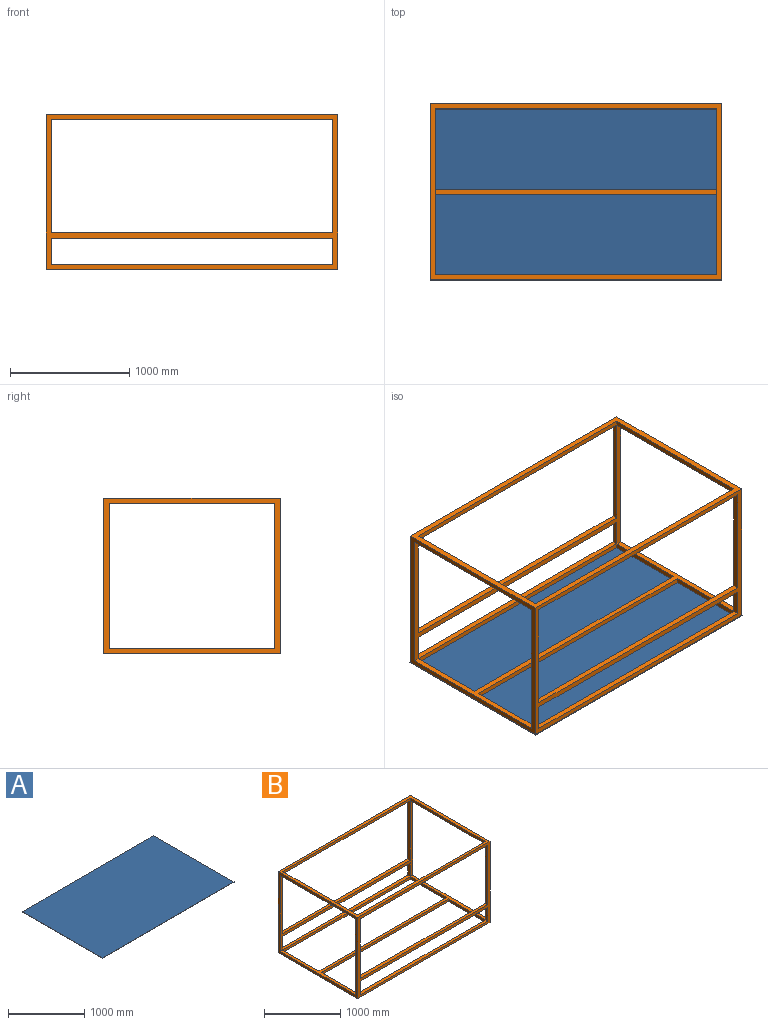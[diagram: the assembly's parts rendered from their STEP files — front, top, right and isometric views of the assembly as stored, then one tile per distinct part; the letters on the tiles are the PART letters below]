
ASSEMBLY  parts=2 mates=1
PART A: 6 faces, bbox 2450x1490x4 mm
  f0: plane 2450x4mm, normal (0,1,0), area 9800mm2, adj f1,f3,f4,f5
  f1: plane 1490x4mm, normal (-1,0,0), area 5960mm2, adj f0,f2,f4,f5
  f2: plane 2450x4mm, normal (0,-1,0), area 9800mm2, adj f1,f3,f4,f5
  f3: plane 1490x4mm, normal (1,0,0), area 5960mm2, adj f0,f2,f4,f5
  f4: plane 2450x1490mm, normal (0,0,1), area 3650500mm2, adj f0,f1,f2,f3
  f5: plane 2450x1490mm, normal (0,0,-1), area 3650500mm2, adj f0,f1,f2,f3
PART B: 39 faces, bbox 2450x1480x1300 mm
  f0: plane 955x45mm, normal (1,0,0), area 42975mm2, adj f14,f20,f26,f37
  f1: plane 955x45mm, normal (-1,0,0), area 42975mm2, adj f14,f20,f26,f37
  f2: plane 220x45mm, normal (1,0,0), area 9900mm2, adj f4,f17,f23,f36
  f3: plane 220x45mm, normal (-1,0,0), area 9900mm2, adj f4,f17,f23,f36
  f4: plane 2360x45mm, normal (0,0,1), area 106200mm2, adj f2,f3,f11,f17
  f5: plane 2450x1390mm, normal (0,0,1), area 231300mm2, adj f7,f9,f10,f12,f13,f15,f16,f18
  f6: plane 2360x45mm, normal (0,0,1), area 106200mm2, adj f8,f14,f21,f24
  f7: plane 670x40mm, normal (1,0,0), area 26800mm2, adj f5,f8,f18,f19
  f8: plane 2360x40mm, normal (0,-1,0), area 94400mm2, adj f6,f7,f9,f19
  f9: plane 670x40mm, normal (-1,0,0), area 26800mm2, adj f5,f8,f18,f19
  f10: plane 675x40mm, normal (-1,0,0), area 27000mm2, adj f5,f11,f16,f19
  f11: plane 2360x40mm, normal (0,1,0), area 94400mm2, adj f4,f10,f12,f19
  f12: plane 675x40mm, normal (1,0,0), area 27000mm2, adj f5,f11,f16,f19
  f13: plane 1480x1300mm, normal (1,0,0), area 228200mm2, adj f5,f14,f17,f19,f20,f23,f29,f34
  f14: plane 2450x1300mm, normal (0,1,0), area 412000mm2, adj f0,f1,f6,f13,f15,f19,f21,f24
  f15: plane 1480x1300mm, normal (-1,0,0), area 228200mm2, adj f5,f14,f17,f19,f20,f23,f28,f34
  f16: plane 2360x40mm, normal (0,-1,0), area 94400mm2, adj f5,f10,f12,f19
  f17: plane 2450x1300mm, normal (0,-1,0), area 412000mm2, adj f2,f3,f4,f13,f15,f19,f22,f25
  f18: plane 2360x40mm, normal (0,1,0), area 94400mm2, adj f5,f7,f9,f19
  f19: plane 2450x1480mm, normal (0,0,-1), area 451800mm2, adj f7,f8,f9,f10,f11,f12,f13,f14
  f20: plane 2450x1220mm, normal (0,-1,0), area 216000mm2, adj f0,f1,f5,f13,f15,f21,f24,f28
  f21: plane 220x45mm, normal (1,0,0), area 9900mm2, adj f6,f14,f20,f38
  f22: plane 955x45mm, normal (1,0,0), area 42975mm2, adj f17,f23,f27,f35
  f23: plane 2450x1220mm, normal (0,1,0), area 216000mm2, adj f2,f3,f5,f13,f15,f22,f25,f28
  f24: plane 220x45mm, normal (-1,0,0), area 9900mm2, adj f6,f14,f20,f38
  f25: plane 955x45mm, normal (-1,0,0), area 42975mm2, adj f17,f23,f27,f35
  f26: plane 2360x45mm, normal (0,0,-1), area 106200mm2, adj f0,f1,f14,f32
  f27: plane 2360x45mm, normal (0,0,-1), area 106200mm2, adj f17,f22,f25,f30
  f28: plane 1390x45mm, normal (0,0,-1), area 62550mm2, adj f15,f20,f23,f31
  f29: plane 1390x45mm, normal (0,0,-1), area 62550mm2, adj f13,f20,f23,f33
  f30: plane 2360x40mm, normal (0,1,0), area 94400mm2, adj f27,f31,f33,f34
  f31: plane 1390x40mm, normal (1,0,0), area 55600mm2, adj f28,f30,f32,f34
  f32: plane 2360x40mm, normal (0,-1,0), area 94400mm2, adj f26,f31,f33,f34
  f33: plane 1390x40mm, normal (-1,0,0), area 55600mm2, adj f29,f30,f32,f34
  f34: plane 2450x1480mm, normal (0,0,1), area 345600mm2, adj f13,f14,f15,f17,f30,f31,f32,f33
  f35: plane 2360x45mm, normal (0,0,1), area 106200mm2, adj f17,f22,f23,f25
  f36: plane 2360x45mm, normal (0,0,-1), area 106200mm2, adj f2,f3,f17,f23
  f37: plane 2360x45mm, normal (0,0,1), area 106200mm2, adj f0,f1,f14,f20
  f38: plane 2360x45mm, normal (0,0,-1), area 106200mm2, adj f14,f20,f21,f24
PLACE A t=(22.41,169.11,-201.89)mm
PLACE B t=(22.41,149.11,-197.89)mm
MATE planar B.f19 <-> A.f4  axis (0,0,-1) through (22.41,149.7,-197.89)mm
